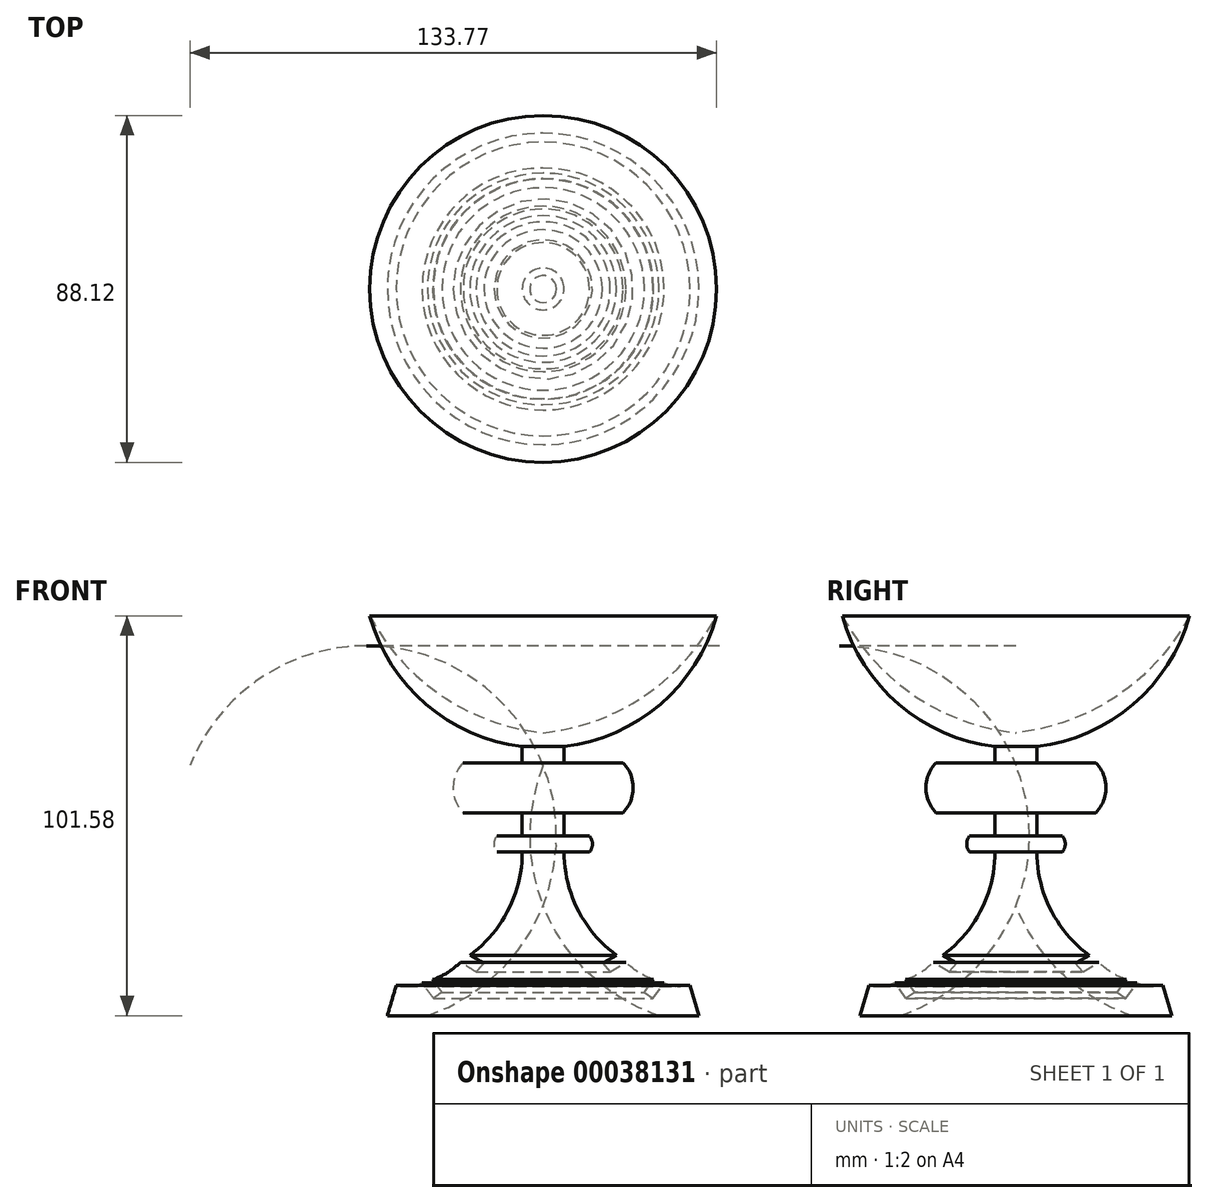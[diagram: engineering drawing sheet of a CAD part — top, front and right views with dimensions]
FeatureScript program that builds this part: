
annotation { "Feature Type Name" : "Feature", "Feature Type Description" : "" }
export const myFeature = defineFeature(function(context is Context, id is Id, definition is map)
    precondition{}
    {
        {
            var Q0;
            Q0=qCreatedBy(makeId("Front.planeOp"),FACE);
            var sketch = newSketch(context, id + "F0", { "sketchPlane" : qUnion([Q0])});
            skLineSegment(sketch, "E0", {"start": v(29.42, 0) * mm, "end": v(39.58, 0) * mm});
            skLineSegment(sketch, "E1", {"start": v(39.58, 0) * mm, "end": v(37.32, 7.72) * mm});
            skLineSegment(sketch, "E2", {"start": v(0, 27.92) * mm, "end": v(0, 68.06) * mm});
            skLineSegment(sketch, "E3", {"start": v(5.31, 43.1) * mm, "end": v(5.31, 68.37) * mm});
            skArc(sketch, "E4", {"start": v(0, 27.92) * mm, "mid": v(11.63, 10.72) * mm, "end": v(29.42, 0) * mm});
            skPoint(sketch, "E5", {"position": v(0, 34.03) * mm});
            skLineSegment(sketch, "E6.bottom", {"start": v(0, 51.55) * mm, "end": v(20.32, 51.55) * mm});
            skLineSegment(sketch, "E6.top", {"start": v(0, 64.25) * mm, "end": v(20.32, 64.25) * mm});
            skLineSegment(sketch, "E6.left", {"start": v(0, 51.55) * mm, "end": v(0, 64.25) * mm});
            skLineSegment(sketch, "E6.right", {"start": v(20.32, 51.55) * mm, "end": v(20.32, 64.25) * mm});
            skArc(sketch, "E7", {"start": v(0, 68.06) * mm, "mid": v(27.68, 77.4) * mm, "end": v(44.06, 101.58) * mm});
            skLineSegment(sketch, "E8", {"start": v(0, 68.06) * mm, "end": v(0, 113.78) * mm});
            skPoint(sketch, "E9.orphan", {"position": v(0, 0) * mm});
            skArc(sketch, "E10", {"start": v(0, 71.87) * mm, "mid": v(25.72, 81.25) * mm, "end": v(44.06, 101.58) * mm});
            skLineSegment(sketch, "E11.left", {"start": v(5.31, 43.1) * mm, "end": v(5.31, 45.62) * mm});
            skLineSegment(sketch, "E12.left", {"start": v(5.31, 49.31) * mm, "end": v(5.31, 52.43) * mm});
            skLineSegment(sketch, "E13.top", {"start": v(5.31, 51.55) * mm, "end": v(20.32, 51.55) * mm});
            skLineSegment(sketch, "E13.left", {"start": v(5.31, 51.55) * mm, "end": v(5.31, 52.43) * mm});
            skLineSegment(sketch, "E13.right", {"start": v(20.32, 51.55) * mm, "end": v(20.32, 65.13) * mm});
            skArc(sketch, "E14", {"start": v(20.32, 51.55) * mm, "mid": v(22.88, 57.9) * mm, "end": v(20.32, 64.25) * mm});
            skLineSegment(sketch, "E15.bottom", {"start": v(5.31, 45.62) * mm, "end": v(11.77, 45.62) * mm});
            skLineSegment(sketch, "E15.top", {"start": v(5.31, 41.6) * mm, "end": v(11.77, 41.6) * mm});
            skLineSegment(sketch, "E15.left", {"start": v(5.31, 45.62) * mm, "end": v(5.31, 41.6) * mm});
            skLineSegment(sketch, "E15.right", {"start": v(11.77, 45.62) * mm, "end": v(11.77, 41.6) * mm});
            skArc(sketch, "E16", {"start": v(11.77, 41.6) * mm, "mid": v(12.51, 43.62) * mm, "end": v(11.77, 45.62) * mm});
            skLineSegment(sketch, "E17", {"start": v(18.62, 15.37) * mm, "end": v(15.04, 13.37) * mm});
            skLineSegment(sketch, "E18", {"start": v(21.02, 13.6) * mm, "end": v(17.02, 11.1) * mm});
            skLineSegment(sketch, "E19", {"start": v(17.02, 11.1) * mm, "end": v(15.04, 13.37) * mm});
            skArc(sketch, "E20", {"start": v(5.31, 41.6) * mm, "mid": v(8.83, 26.9) * mm, "end": v(18.62, 15.37) * mm});
            skLineSegment(sketch, "E21", {"start": v(28.04, 9.16) * mm, "end": v(25.72, 5.98) * mm});
            skLineSegment(sketch, "E22", {"start": v(25.72, 5.98) * mm, "end": v(27.9, 4.4) * mm});
            skLineSegment(sketch, "E23", {"start": v(27.9, 4.4) * mm, "end": v(30.75, 8.3) * mm});
            skArc(sketch, "E24", {"start": v(21.02, 13.6) * mm, "mid": v(24.27, 10.96) * mm, "end": v(28.04, 9.16) * mm});
            skArc(sketch, "E25", {"start": v(30.75, 8.3) * mm, "mid": v(33.98, 7.44) * mm, "end": v(37.32, 7.72) * mm});
            skSolve(sketch);
        }
        {
            var Q0;
            Q0 = qSketchRegion(id + "F0", true);
            var Q1;
            Q1=sQuery(id+"F0.wireOp",EDGE,"E2");
            revolve(context, id + "F1", {"entities" : qUnion([Q0]), "axis" : qUnion([Q1]), "revolveType" : RevolveType.FULL});
        }
    });
